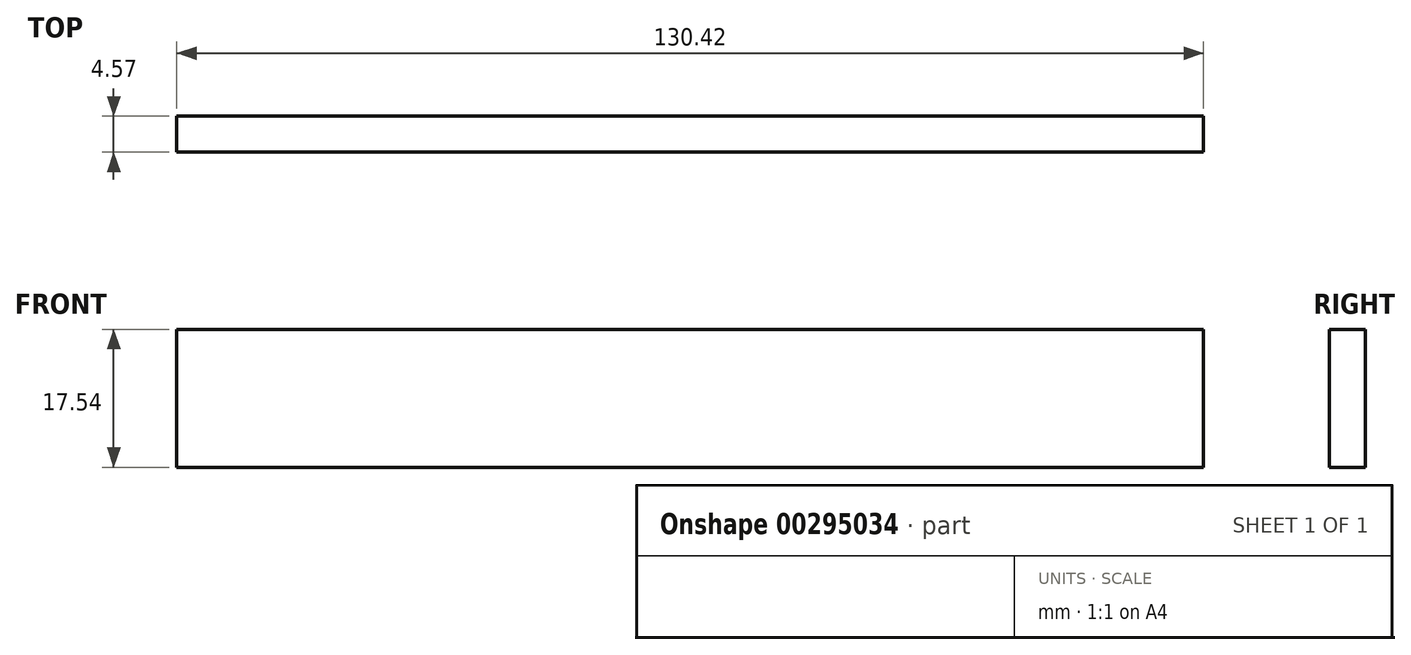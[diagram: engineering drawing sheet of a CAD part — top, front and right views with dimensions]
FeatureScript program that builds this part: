
annotation { "Feature Type Name" : "Feature", "Feature Type Description" : "" }
export const myFeature = defineFeature(function(context is Context, id is Id, definition is map)
    precondition{}
    {
        {
            var Q0;
            Q0=qCreatedBy(makeId("Front.planeOp"),FACE);
            var sketch = newSketch(context, id + "F0", { "sketchPlane" : qUnion([Q0])});
            skLineSegment(sketch, "E0.bottom", {"start": v(65.21, 8.77) * mm, "end": v(-65.21, 8.77) * mm});
            skLineSegment(sketch, "E0.top", {"start": v(65.21, -8.77) * mm, "end": v(-65.21, -8.77) * mm});
            skLineSegment(sketch, "E0.left", {"start": v(65.21, 8.77) * mm, "end": v(65.21, -8.77) * mm});
            skLineSegment(sketch, "E0.right", {"start": v(-65.21, 8.77) * mm, "end": v(-65.21, -8.77) * mm});
            skPoint(sketch, "E0.middle", {"position": v(0, 0) * mm});
            skSolve(sketch);
        }
        {
            var Q0;
            Q0=makeQuery(id+"F0.imprint","IMPRINT",FACE,{"disambiguationData":[TD([[makeQuery(id+"F0.imprint","IMPRINT",EDGE,{"derivedFrom":sQuery(id+"F0.wireOp",EDGE,"E0.bottom")}),1.0]])]});
            extrude(context, id + "F1", {"entities" : qUnion([Q0]), "depth" : 4.57 * mm});
        }
        {
            var Q0;
            Q0=makeQuery(id+"F1.opExtrude","SWEPT_FACE",FACE,{"disambiguationData":[OSD([sQuery(id+"F0.wireOp",EDGE,"E0.left")])]});
            extrude(context, id + "F2", {"entities" : qUnion([Q0]), "operationType" : NewBodyOperationType.ADD, "oppositeDirection" : true, "depth" : 24.9 * mm});
        }
    });
